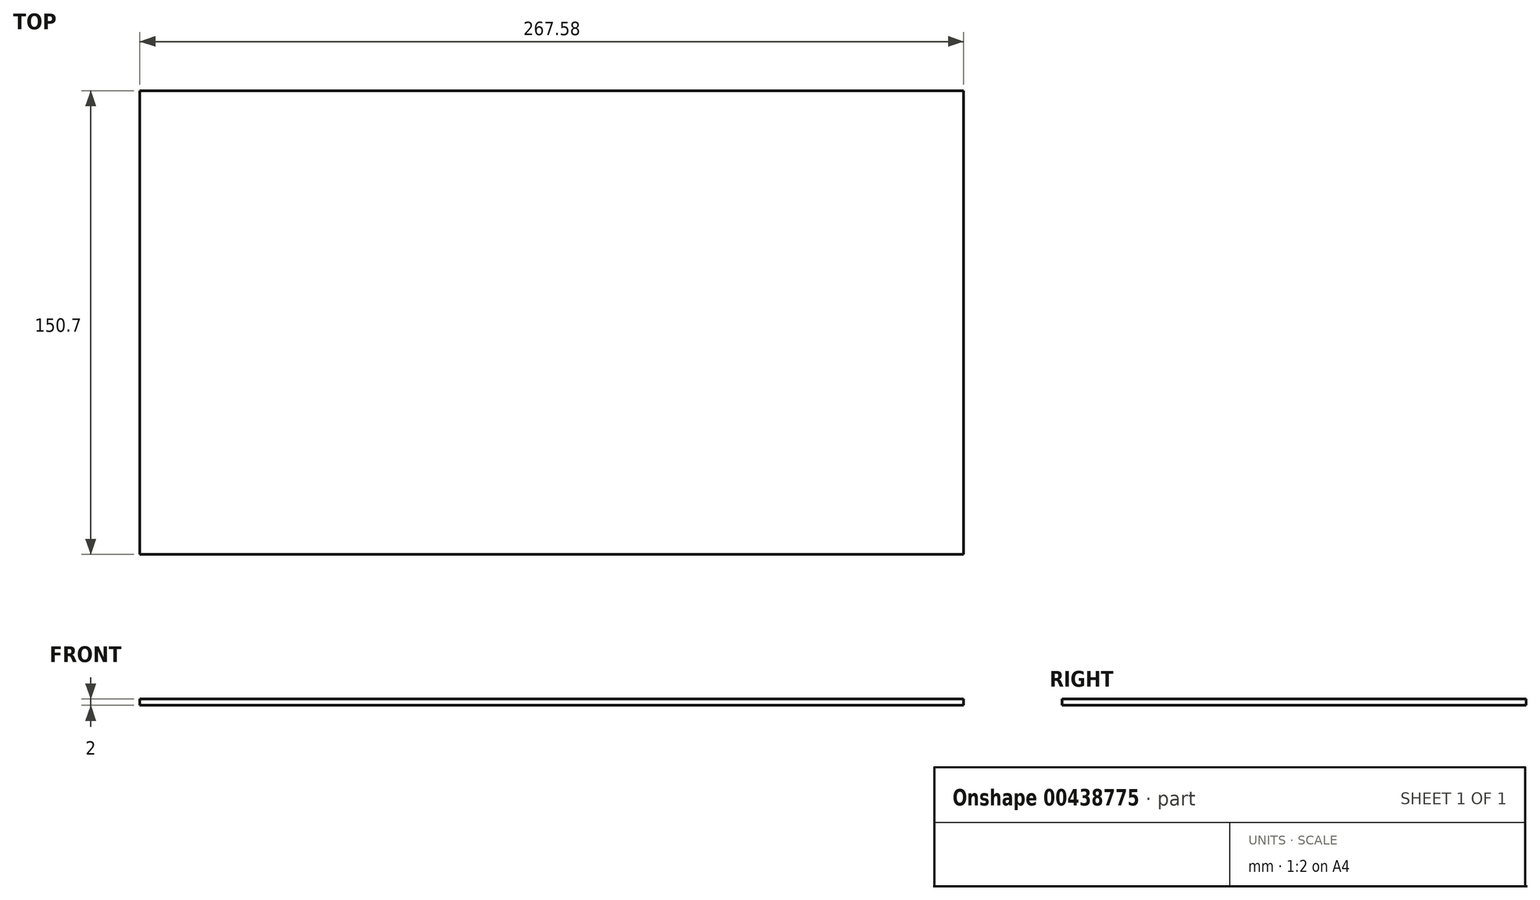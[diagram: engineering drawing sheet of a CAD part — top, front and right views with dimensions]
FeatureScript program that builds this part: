
annotation { "Feature Type Name" : "Feature", "Feature Type Description" : "" }
export const myFeature = defineFeature(function(context is Context, id is Id, definition is map)
    precondition{}
    {
        {
            var Q0;
            Q0=qCreatedBy(makeId("Top.planeOp"),FACE);
            var sketch = newSketch(context, id + "F0", { "sketchPlane" : qUnion([Q0])});
            skLineSegment(sketch, "E0.bottom", {"start": v(133.8, 75.35) * mm, "end": v(-133.8, 75.35) * mm});
            skLineSegment(sketch, "E0.top", {"start": v(133.8, -75.35) * mm, "end": v(-133.8, -75.35) * mm});
            skLineSegment(sketch, "E0.left", {"start": v(133.8, 75.35) * mm, "end": v(133.8, -75.35) * mm});
            skLineSegment(sketch, "E0.right", {"start": v(-133.8, 75.35) * mm, "end": v(-133.8, -75.35) * mm});
            skPoint(sketch, "E0.middle", {"position": v(0, 0) * mm});
            skLineSegment(sketch, "E1", {"start": v(-133.8, -75.35) * mm, "end": v(133.8, 75.35) * mm, "construction": true});
            skSolve(sketch);
        }
        {
            var Q0;
            Q0=makeQuery(id+"F0.imprint","IMPRINT",FACE,{"disambiguationData":[TD([[makeQuery(id+"F0.imprint","IMPRINT",EDGE,{"derivedFrom":sQuery(id+"F0.wireOp",EDGE,"E0.bottom")}),1.0]])]});
            extrude(context, id + "F1", {"entities" : qUnion([Q0]), "depth" : 2 * mm});
        }
    });
